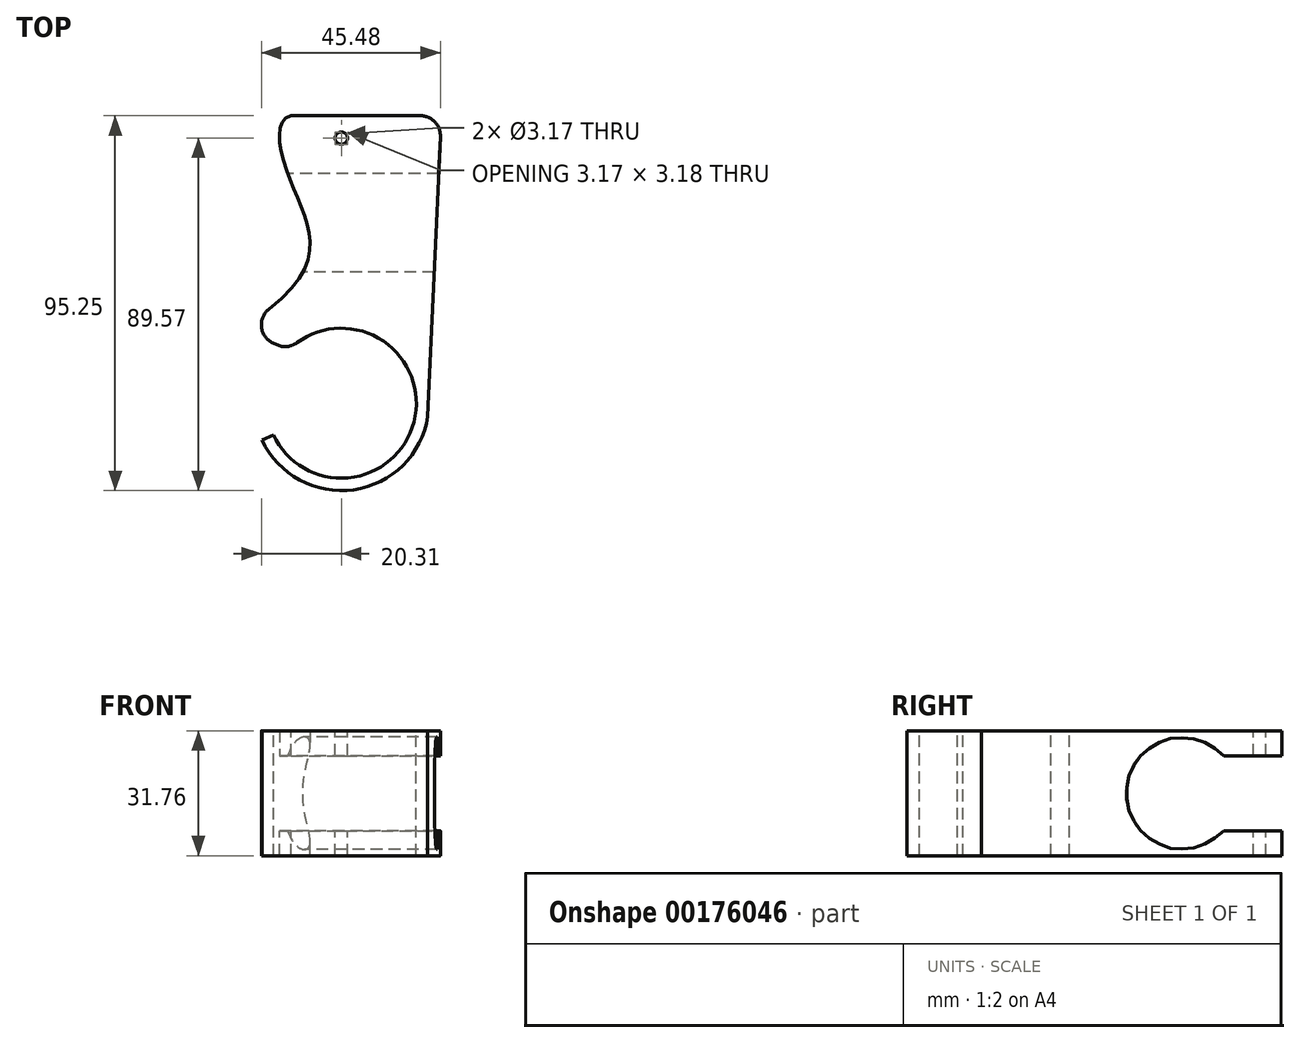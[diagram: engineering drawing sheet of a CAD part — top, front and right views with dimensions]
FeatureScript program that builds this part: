
annotation { "Feature Type Name" : "Feature", "Feature Type Description" : "" }
export const myFeature = defineFeature(function(context is Context, id is Id, definition is map)
    precondition{}
    {
        {
            var Q0;
            Q0=qCreatedBy(makeId("Right.planeOp"),FACE);
            var sketch = newSketch(context, id + "F0", { "sketchPlane" : qUnion([Q0])});
            skCircle(sketch, "E0", {"center": v(0, 0) * mm, "radius": 14.29 * mm});
            skSolve(sketch);
        }
        {
            var Q0;
            Q0=qCreatedBy(makeId("Right.planeOp"),FACE);
            var sketch = newSketch(context, id + "F1", { "sketchPlane" : qUnion([Q0])});
            skCircle(sketch, "E1", {"center": v(0, 0) * mm, "radius": 14.29 * mm});
            skLineSegment(sketch, "E2.bottom", {"start": v(-25.4, 15.88) * mm, "end": v(25.4, 15.88) * mm});
            skLineSegment(sketch, "E2.top", {"start": v(-25.4, -15.88) * mm, "end": v(25.4, -15.88) * mm});
            skLineSegment(sketch, "E2.left", {"start": v(-25.4, 15.88) * mm, "end": v(-25.4, -15.88) * mm});
            skLineSegment(sketch, "E2.right", {"start": v(25.4, 15.88) * mm, "end": v(25.4, -15.88) * mm});
            skCircle(sketch, "E3", {"center": v(0, 0) * mm, "radius": 15.88 * mm});
            skLineSegment(sketch, "E4", {"start": v(-28.58, 15.88) * mm, "end": v(-28.58, -15.88) * mm});
            skLineSegment(sketch, "E5", {"start": v(-25.4, 15.88) * mm, "end": v(-28.58, 15.88) * mm});
            skLineSegment(sketch, "E6", {"start": v(-28.58, -15.88) * mm, "end": v(-25.4, -15.88) * mm});
            skSolve(sketch);
        }
        {
            var Q0;
            {var subQ0=sQuery(id+"F1.wireOp",EDGE,"E2.right");Q0=makeQuery(id+"F1.imprint","IMPRINT",FACE,{"disambiguationData":[TD([[makeQuery(id+"F1.imprint","IMPRINT",EDGE,{"derivedFrom":subQ0}),-1.0]])]});}
            var Q1;
            {var subQ0=sQuery(id+"F1.wireOp",EDGE,"E2.bottom");var subQ1=sQuery(id+"F1.wireOp",EDGE,"E1");var subQ2=makeQuery(id+"F1.imprint","INTERSECT",VERTEX,{"derivedFrom":[subQ1,subQ0]});Q1=makeQuery(id+"F1.imprint","IMPRINT",FACE,{"disambiguationData":[TD([[makeQuery(id+"F1.imprint","IMPRINT",EDGE,{"disambiguationData":[TD([[subQ2,1.0]])],"derivedFrom":subQ1}),-1.0]])]});}
            var Q2;
            {var subQ0=sQuery(id+"F1.wireOp",EDGE,"E3");var subQ1=sQuery(id+"F1.wireOp",EDGE,"E2.bottom");var subQ2=makeQuery(id+"F1.imprint","INTERSECT",VERTEX,{"disambiguationData":[OD(0.0)],"derivedFrom":[subQ1,subQ0]});Q2=makeQuery(id+"F1.imprint","IMPRINT",FACE,{"disambiguationData":[TD([[makeQuery(id+"F1.imprint","IMPRINT",EDGE,{"disambiguationData":[TD([[subQ2,-1.0]])],"derivedFrom":subQ1}),1.0]])]});}
            var Q3;
            {var subQ0=sQuery(id+"F1.wireOp",EDGE,"E2.left");Q3=makeQuery(id+"F1.imprint","IMPRINT",FACE,{"disambiguationData":[TD([[makeQuery(id+"F1.imprint","IMPRINT",EDGE,{"derivedFrom":subQ0}),1.0]])]});}
            var Q4;
            {var subQ0=sQuery(id+"F1.wireOp",EDGE,"E3");var subQ1=sQuery(id+"F1.wireOp",EDGE,"E2.top");var subQ2=makeQuery(id+"F1.imprint","INTERSECT",VERTEX,{"disambiguationData":[OD(0.0)],"derivedFrom":[subQ1,subQ0]});Q4=makeQuery(id+"F1.imprint","IMPRINT",FACE,{"disambiguationData":[TD([[makeQuery(id+"F1.imprint","IMPRINT",EDGE,{"disambiguationData":[TD([[subQ2,-1.0]])],"derivedFrom":subQ1}),-1.0]])]});}
            var Q5;
            {var subQ0=sQuery(id+"F1.wireOp",EDGE,"E2.bottom");var subQ1=sQuery(id+"F1.wireOp",EDGE,"E1");var subQ2=makeQuery(id+"F1.imprint","INTERSECT",VERTEX,{"derivedFrom":[subQ1,subQ0]});Q5=makeQuery(id+"F1.imprint","IMPRINT",FACE,{"disambiguationData":[TD([[makeQuery(id+"F1.imprint","IMPRINT",EDGE,{"disambiguationData":[TD([[subQ2,-1.0]])],"derivedFrom":subQ1}),-1.0]])]});}
            var Q6;
            {var subQ0=sQuery(id+"F1.wireOp",EDGE,"E4");Q6=makeQuery(id+"F1.imprint","IMPRINT",FACE,{"disambiguationData":[TD([[makeQuery(id+"F1.imprint","IMPRINT",EDGE,{"derivedFrom":subQ0}),1.0]])]});}
            extrude(context, id + "F2", {"entities" : qUnion([Q0, Q1, Q2, Q3, Q4, Q5, Q6]), "endBound" : BoundingType.SYMMETRIC, "depth" : 50.8 * mm});
        }
        {
            var Q0;
            Q0=makeQuery(id+"F2.opExtrude","CAP_FACE",FACE,{"disambiguationData":[OSD([sQuery(id+"F1.wireOp",EDGE,"E1"),sQuery(id+"F1.wireOp",EDGE,"E2.bottom"),sQuery(id+"F1.wireOp",EDGE,"E2.top"),sQuery(id+"F1.wireOp",EDGE,"E2.left"),sQuery(id+"F1.wireOp",EDGE,"E2.right"),sQuery(id+"F1.wireOp",EDGE,"E3")])],"isStart":false});
            var sketch = newSketch(context, id + "F3", { "sketchPlane" : qUnion([Q0])});
            skLineSegment(sketch, "E7.bottom", {"start": v(0, 9.53) * mm, "end": v(25.4, 9.53) * mm});
            skLineSegment(sketch, "E7.top", {"start": v(0, -9.53) * mm, "end": v(25.4, -9.53) * mm});
            skLineSegment(sketch, "E7.left", {"start": v(0, 9.53) * mm, "end": v(0, -9.53) * mm});
            skLineSegment(sketch, "E7.right", {"start": v(25.4, 9.53) * mm, "end": v(25.4, -9.53) * mm});
            skPoint(sketch, "E7.middle", {"position": v(12.7, 0) * mm});
            skSolve(sketch);
        }
        {
            var Q0;
            {var subQ0=sQuery(id+"F3.wireOp",EDGE,"E7.left");Q0=makeQuery(id+"F3.imprint","IMPRINT",FACE,{"disambiguationData":[TD([[makeQuery(id+"F3.imprint","IMPRINT",EDGE,{"derivedFrom":subQ0}),1.0]])]});}
            var Q1;
            {var subQ0=sQuery(id+"F3.wireOp",EDGE,"E7.right");Q1=makeQuery(id+"F3.imprint","IMPRINT",FACE,{"disambiguationData":[TD([[makeQuery(id+"F3.imprint","IMPRINT",EDGE,{"derivedFrom":subQ0}),-1.0]])]});}
            extrude(context, id + "F4", {"entities" : qUnion([Q0, Q1]), "operationType" : NewBodyOperationType.REMOVE, "endBound" : BoundingType.THROUGH_ALL, "oppositeDirection" : true, "depth" : 25.4 * mm});
        }
        {
            var Q0;
            {var subQ0=sQuery(id+"F1.wireOp",EDGE,"E2.bottom");Q0=makeQuery(id+"F2.opExtrude","SWEPT_FACE",FACE,{"disambiguationData":[OSD([subQ0]),TDD([makeQuery(id+"F1.imprint","IMPRINT",EDGE,{"disambiguationData":[TD([[makeQuery(id+"F1.imprint","INTERSECT",VERTEX,{"derivedFrom":[subQ0,sQuery(id+"F1.wireOp",EDGE,"E4")]}),-1.0]])],"derivedFrom":subQ0})])]});}
            var sketch = newSketch(context, id + "F5", { "sketchPlane" : qUnion([Q0])});
            skCircle(sketch, "E8", {"center": v(0, -47.63) * mm, "radius": 19.05 * mm});
            skCircle(sketch, "E9", {"center": v(0, -47.63) * mm, "radius": 22.23 * mm});
            skLineSegment(sketch, "E10", {"start": v(0, -47.63) * mm, "end": v(-15.72, -31.9) * mm});
            skLineSegment(sketch, "E11", {"start": v(0, -47.63) * mm, "end": v(-20.14, -57.02) * mm});
            skSolve(sketch);
        }
        {
            var Q0;
            {var subQ0=sQuery(id+"F5.wireOp",EDGE,"E10");var subQ1=sQuery(id+"F5.wireOp",EDGE,"E9");var subQ2=makeQuery(id+"F5.imprint","INTERSECT",VERTEX,{"derivedFrom":[subQ1,subQ0]});Q0=makeQuery(id+"F5.imprint","IMPRINT",FACE,{"disambiguationData":[TD([[makeQuery(id+"F5.imprint","IMPRINT",EDGE,{"disambiguationData":[TD([[subQ2,1.0]])],"derivedFrom":subQ0}),-1.0]])]});}
            var Q1;
            {var subQ7=sQuery(id+"F5.wireOp",EDGE,"E11");var subQ8=sQuery(id+"F5.wireOp",EDGE,"E9");var subQ9=makeQuery(id+"F5.imprint","INTERSECT",VERTEX,{"derivedFrom":[subQ8,subQ7]});Q1=makeQuery(id+"F5.imprint","IMPRINT",FACE,{"disambiguationData":[TD([[makeQuery(id+"F5.imprint","IMPRINT",EDGE,{"disambiguationData":[TD([[subQ9,1.0]])],"derivedFrom":subQ7}),1.0]])]});}
            var Q2;
            {var subQ0=sQuery(id+"F1.wireOp",EDGE,"E2.top");Q2=makeQuery(id+"F2.opExtrude","SWEPT_FACE",FACE,{"disambiguationData":[OSD([subQ0]),TDD([makeQuery(id+"F1.imprint","IMPRINT",EDGE,{"disambiguationData":[TD([[makeQuery(id+"F1.imprint","INTERSECT",VERTEX,{"derivedFrom":[subQ0,sQuery(id+"F1.wireOp",EDGE,"E4")]}),-1.0]])],"derivedFrom":subQ0})])]});}
            extrude(context, id + "F6", {"entities" : qUnion([Q0, Q1]), "operationType" : NewBodyOperationType.ADD, "endBound" : BoundingType.UP_TO_SURFACE, "oppositeDirection" : true, "endBoundEntityFace" : qUnion([Q2]), "depth" : 25.4 * mm});
        }
        {
            var Q0;
            {var subQ0=sQuery(id+"F1.wireOp",EDGE,"E2.bottom");Q0=makeQuery(id+"F2.opExtrude","SWEPT_FACE",FACE,{"disambiguationData":[OSD([subQ0]),TDD([makeQuery(id+"F1.imprint","IMPRINT",EDGE,{"disambiguationData":[TD([[makeQuery(id+"F1.imprint","INTERSECT",VERTEX,{"derivedFrom":[subQ0,sQuery(id+"F1.wireOp",EDGE,"E2.right")]}),1.0]])],"derivedFrom":subQ0})])]});}
            var sketch = newSketch(context, id + "F7", { "sketchPlane" : qUnion([Q0])});
            skCircle(sketch, "E12", {"center": v(0, 19.72) * mm, "radius": 1.59 * mm});
            skSolve(sketch);
        }
        {
            var Q0;
            Q0=makeQuery(id+"F7.imprint","IMPRINT",FACE,{"disambiguationData":[TD([[makeQuery(id+"F7.imprint","IMPRINT",EDGE,{"derivedFrom":sQuery(id+"F7.wireOp",EDGE,"E12")}),1.0]])]});
            extrude(context, id + "F8", {"entities" : qUnion([Q0]), "operationType" : NewBodyOperationType.REMOVE, "endBound" : BoundingType.THROUGH_ALL, "oppositeDirection" : true, "depth" : 25.4 * mm});
        }
        {
            var Q0;
            {var subQ0=sQuery(id+"F5.wireOp",EDGE,"E9");var subQ1=sQuery(id+"F5.wireOp",EDGE,"E8");var subQ2=sQuery(id+"F1.wireOp",EDGE,"E5");var subQ3=sQuery(id+"F1.wireOp",EDGE,"E4");Q0=makeQuery(id+"F6.boolean.opBoolean","MERGE",FACE,{"derivedFrom":[makeQuery(id+"F2.opExtrude","SWEPT_FACE",FACE,{"disambiguationData":[OSD([sQuery(id+"F1.wireOp",EDGE,"E2.bottom"),subQ2])]}),makeQuery(id+"F6.opExtrude","CAP_FACE",FACE,{"disambiguationData":[OSD([subQ3,subQ2,subQ1,subQ0,sQuery(id+"F5.wireOp",EDGE,"E10")])],"isStart":true}),makeQuery(id+"F6.opExtrude","CAP_FACE",FACE,{"disambiguationData":[OSD([subQ3,subQ2,subQ1,subQ0,sQuery(id+"F5.wireOp",EDGE,"E11")])],"isStart":true})]});}
            var sketch = newSketch(context, id + "F9", { "sketchPlane" : qUnion([Q0])});
            skLineSegment(sketch, "E13", {"start": v(25.4, -28.58) * mm, "end": v(21.97, -50.99) * mm});
            skLineSegment(sketch, "E14", {"start": v(-25.4, -28.58) * mm, "end": v(-13.47, -34.15) * mm});
            skSolve(sketch);
        }
        {
            var Q0;
            Q0 = qSketchRegion(id + "F9", true);
            var Q1;
            {var subQ1=sQuery(id+"F5.wireOp",EDGE,"E10");var subQ2=sQuery(id+"F5.wireOp",EDGE,"E9");var subQ4=sQuery(id+"F1.wireOp",EDGE,"E5");var subQ5=sQuery(id+"F1.wireOp",EDGE,"E4");var subQ6=makeQuery(id+"F2.opExtrude","SWEPT_EDGE",EDGE,{"disambiguationData":[OSD([subQ5,subQ4])]});var subQ7=makeQuery(id+"F5.imprint","IMPRINT",EDGE,{"disambiguationData":[TD([[makeQuery(id+"F5.imprint","INTERSECT",VERTEX,{"derivedFrom":[subQ2,subQ1]}),1.0]])],"derivedFrom":subQ2});var subQ9=makeQuery(id+"F6.boolean.opBoolean","SPLIT",EDGE,{"disambiguationData":[TD([makeQuery(id+"F6.opExtrude","SWEPT_FACE",FACE,{"disambiguationData":[OSD([subQ2]),TDD([subQ7])]})])],"derivedFrom":subQ6});Q1=makeQuery(id+"F9.imprint","IMPRINT",FACE,{"disambiguationData":[TD([[makeQuery(id+"F9.imprint","IMPRINT",EDGE,{"derivedFrom":subQ9}),1.0]])]});}
            var Q2;
            {var subQ0=sQuery(id+"F9.wireOp",EDGE,"E13");Q2=makeQuery(id+"F9.imprint","IMPRINT",FACE,{"disambiguationData":[TD([[makeQuery(id+"F9.imprint","IMPRINT",EDGE,{"derivedFrom":subQ0}),-1.0]])]});}
            var Q3;
            {var subQ0=sQuery(id+"F5.wireOp",EDGE,"E9");var subQ1=sQuery(id+"F5.wireOp",EDGE,"E8");var subQ2=sQuery(id+"F1.wireOp",EDGE,"E5");var subQ3=sQuery(id+"F1.wireOp",EDGE,"E4");var subQ4=sQuery(id+"F1.wireOp",EDGE,"E6");var subQ5=sQuery(id+"F1.wireOp",EDGE,"E2.top");Q3=makeQuery(id+"F6.boolean.opBoolean","MERGE",FACE,{"derivedFrom":[makeQuery(id+"F2.opExtrude","SWEPT_FACE",FACE,{"disambiguationData":[OSD([subQ5,subQ4])]}),makeQuery(id+"F6.opExtrude","CAP_FACE",FACE,{"disambiguationData":[OSD([subQ5,subQ4]),ownerDisambiguation([makeQuery(id+"F6.opExtrude","SWEPT_BODY",BODY,{"disambiguationData":[OSD([subQ3,subQ2,subQ1,subQ0,sQuery(id+"F5.wireOp",EDGE,"E10")])]})])],"isStart":false}),makeQuery(id+"F6.opExtrude","CAP_FACE",FACE,{"disambiguationData":[OSD([subQ5,subQ4]),ownerDisambiguation([makeQuery(id+"F6.opExtrude","SWEPT_BODY",BODY,{"disambiguationData":[OSD([subQ3,subQ2,subQ1,subQ0,sQuery(id+"F5.wireOp",EDGE,"E11")])]})])],"isStart":false})]});}
            extrude(context, id + "F10", {"entities" : qUnion([Q0, Q1, Q2]), "operationType" : NewBodyOperationType.ADD, "endBound" : BoundingType.UP_TO_SURFACE, "oppositeDirection" : true, "endBoundEntityFace" : qUnion([Q3]), "depth" : 25.4 * mm});
        }
        {
            var Q0;
            {var subQ0=sQuery(id+"F5.wireOp",EDGE,"E9");var subQ1=sQuery(id+"F1.wireOp",EDGE,"E5");var subQ2=sQuery(id+"F1.wireOp",EDGE,"E4");var subQ3=sQuery(id+"F5.wireOp",EDGE,"E8");Q0=makeQuery(id+"F10.boolean.opBoolean","MERGE",FACE,{"derivedFrom":[makeQuery(id+"F6.boolean.opBoolean","MERGE",FACE,{"derivedFrom":[makeQuery(id+"F2.opExtrude","SWEPT_FACE",FACE,{"disambiguationData":[OSD([sQuery(id+"F1.wireOp",EDGE,"E2.bottom"),subQ1])]}),makeQuery(id+"F6.opExtrude","CAP_FACE",FACE,{"disambiguationData":[OSD([subQ2,subQ1,subQ3,subQ0,sQuery(id+"F5.wireOp",EDGE,"E10")])],"isStart":true}),makeQuery(id+"F6.opExtrude","CAP_FACE",FACE,{"disambiguationData":[OSD([subQ2,subQ1,subQ3,subQ0,sQuery(id+"F5.wireOp",EDGE,"E11")])],"isStart":true})]}),makeQuery(id+"F10.opExtrude","CAP_FACE",FACE,{"disambiguationData":[OSD([subQ2,subQ1,subQ0,sQuery(id+"F9.wireOp",EDGE,"vnx9pd8C-HjGg-3WXh-8BVK-Msj8Zm1Jhp6u")])],"isStart":true}),makeQuery(id+"F10.opExtrude","CAP_FACE",FACE,{"disambiguationData":[OSD([subQ2,subQ1,subQ0,sQuery(id+"F9.wireOp",EDGE,"E13")])],"isStart":true})]});}
            var sketch = newSketch(context, id + "F11", { "sketchPlane" : qUnion([Q0])});
            skLineSegment(sketch, "E15", {"start": v(25.4, 25.4) * mm, "end": v(21.97, -50.99) * mm});
            skSolve(sketch);
        }
        {
            var Q0;
            Q0 = qSketchRegion(id + "F11", true);
            var Q1;
            Q1=makeQuery(id+"F11.imprint","IMPRINT",FACE,{"disambiguationData":[TD([[makeQuery(id+"F11.imprint","IMPRINT",EDGE,{"derivedFrom":sQuery(id+"F11.wireOp",EDGE,"pskV8I0j-hnk2-iIVi-R23I-b5Myljy8wFEx")}),-1.0]])]});
            var Q2;
            Q2=makeQuery(id+"F11.imprint","IMPRINT",FACE,{"disambiguationData":[TD([[makeQuery(id+"F11.imprint","IMPRINT",EDGE,{"derivedFrom":sQuery(id+"F11.wireOp",EDGE,"E15")}),1.0]])]});
            extrude(context, id + "F12", {"entities" : qUnion([Q0, Q1, Q2]), "operationType" : NewBodyOperationType.REMOVE, "endBound" : BoundingType.THROUGH_ALL, "oppositeDirection" : true, "depth" : 25.4 * mm});
        }
        {
            var Q0;
            {var subQ0=sQuery(id+"F5.wireOp",EDGE,"E10");var subQ1=sQuery(id+"F5.wireOp",EDGE,"E8");Q0=makeQuery(id+"F10.boolean.opBoolean","MERGE",EDGE,{"derivedFrom":[makeQuery(id+"F6.opExtrude","SWEPT_EDGE",EDGE,{"disambiguationData":[OSD([subQ1,subQ0])]}),makeQuery(id+"F10.opExtrude","SWEPT_EDGE",EDGE,{"disambiguationData":[OSD([subQ1,subQ0,sQuery(id+"F9.wireOp",EDGE,"E14")])]})]});}
            fillet(context, id + "F13", {"entities" : qUnion([Q0]), "radius" : 5.08 * mm, "tangentPropagation" : true, "allowEdgeOverflow" : false});
        }
        {
            var Q0;
            {var subQ0=sQuery(id+"F5.wireOp",EDGE,"E10");var subQ1=sQuery(id+"F5.wireOp",EDGE,"E9");var subQ2=sQuery(id+"F1.wireOp",EDGE,"E5");var subQ3=sQuery(id+"F1.wireOp",EDGE,"E4");var subQ4=sQuery(id+"F5.wireOp",EDGE,"E8");Q0=makeQuery(id+"F10.boolean.opBoolean","MERGE",FACE,{"derivedFrom":[makeQuery(id+"F6.boolean.opBoolean","MERGE",FACE,{"derivedFrom":[makeQuery(id+"F2.opExtrude","SWEPT_FACE",FACE,{"disambiguationData":[OSD([sQuery(id+"F1.wireOp",EDGE,"E2.bottom"),subQ2])]}),makeQuery(id+"F6.opExtrude","CAP_FACE",FACE,{"disambiguationData":[OSD([subQ3,subQ2,subQ4,subQ1,subQ0])],"isStart":true}),makeQuery(id+"F6.opExtrude","CAP_FACE",FACE,{"disambiguationData":[OSD([subQ3,subQ2,subQ4,subQ1,sQuery(id+"F5.wireOp",EDGE,"E11")])],"isStart":true})]}),makeQuery(id+"F10.opExtrude","CAP_FACE",FACE,{"disambiguationData":[OSD([subQ3,subQ2,subQ1,sQuery(id+"F9.wireOp",EDGE,"E13")])],"isStart":true}),makeQuery(id+"F10.opExtrude","CAP_FACE",FACE,{"disambiguationData":[OSD([subQ3,subQ2,subQ1,subQ0,sQuery(id+"F9.wireOp",EDGE,"E14")])],"isStart":true})]});}
            var sketch = newSketch(context, id + "F14", { "sketchPlane" : qUnion([Q0])});
            skFitSpline(sketch, "E16", {"points": [v(-11.59, 25.56) * mm, v(-12.62, 8.06) * mm, v(-25.4, -28.58) * mm], "startDerivative": vector(-48.35, -1.23) * mm, "endDerivative": vector(-122.94, -76.25) * mm});
            skSolve(sketch);
        }
        {
            var Q0;
            Q0=makeQuery(id+"F14.imprint","IMPRINT",FACE,{"disambiguationData":[TD([[makeQuery(id+"F14.imprint","IMPRINT",EDGE,{"derivedFrom":sQuery(id+"F14.wireOp",EDGE,"E16")}),-1.0]])]});
            extrude(context, id + "F15", {"entities" : qUnion([Q0]), "operationType" : NewBodyOperationType.REMOVE, "endBound" : BoundingType.THROUGH_ALL, "oppositeDirection" : true, "depth" : 25.4 * mm});
        }
        {
            var Q0;
            {var subQ0=sQuery(id+"F9.wireOp",EDGE,"E14");var subQ1=sQuery(id+"F1.wireOp",EDGE,"E5");var subQ2=sQuery(id+"F1.wireOp",EDGE,"E2.bottom");var subQ3=sQuery(id+"F1.wireOp",EDGE,"E4");Q0=makeQuery(id+"F15.boolean.opBoolean","MERGE",EDGE,{"derivedFrom":[makeQuery(id+"F10.boolean.opBoolean","MERGE",EDGE,{"derivedFrom":[makeQuery(id+"F2.opExtrude","CAP_EDGE",EDGE,{"disambiguationData":[OSD([subQ3])],"isStart":true}),makeQuery(id+"F10.opExtrude","SWEPT_EDGE",EDGE,{"disambiguationData":[OSD([subQ2,subQ3,subQ1,subQ0])]})]}),makeQuery(id+"F15.opExtrude","SWEPT_EDGE",EDGE,{"disambiguationData":[OSD([subQ2,subQ1,subQ0,sQuery(id+"F14.wireOp",EDGE,"E16")])]})]});}
            fillet(context, id + "F16", {"entities" : qUnion([Q0]), "radius" : 5.08 * mm, "tangentPropagation" : true, "allowEdgeOverflow" : false});
        }
        {
            var Q0;
            {var subQ0=sQuery(id+"F1.wireOp",EDGE,"E5");var subQ1=sQuery(id+"F1.wireOp",EDGE,"E2.right");var subQ2=sQuery(id+"F1.wireOp",EDGE,"E2.bottom");Q0=makeQuery(id+"F12.boolean.opBoolean","MERGE",EDGE,{"derivedFrom":[makeQuery(id+"F4.boolean.opBoolean","SPLIT",EDGE,{"disambiguationData":[TD([makeQuery(id+"F4.opExtrude","SWEPT_FACE",FACE,{"disambiguationData":[OSD([sQuery(id+"F3.wireOp",EDGE,"E7.bottom")])]})])],"derivedFrom":makeQuery(id+"F2.opExtrude","CAP_EDGE",EDGE,{"disambiguationData":[OSD([subQ1])],"isStart":false})}),makeQuery(id+"F12.opExtrude","SWEPT_EDGE",EDGE,{"disambiguationData":[OSD([subQ2,subQ1,subQ0,sQuery(id+"F11.wireOp",EDGE,"E15")])]})]});}
            var Q1;
            {var subQ0=sQuery(id+"F1.wireOp",EDGE,"E5");var subQ1=sQuery(id+"F1.wireOp",EDGE,"E2.right");var subQ2=sQuery(id+"F1.wireOp",EDGE,"E2.bottom");Q1=makeQuery(id+"F12.boolean.opBoolean","MERGE",EDGE,{"derivedFrom":[makeQuery(id+"F4.boolean.opBoolean","SPLIT",EDGE,{"disambiguationData":[TD([makeQuery(id+"F4.opExtrude","SWEPT_FACE",FACE,{"disambiguationData":[OSD([sQuery(id+"F3.wireOp",EDGE,"E7.top")])]})])],"derivedFrom":makeQuery(id+"F2.opExtrude","CAP_EDGE",EDGE,{"disambiguationData":[OSD([subQ1])],"isStart":false})}),makeQuery(id+"F12.opExtrude","SWEPT_EDGE",EDGE,{"disambiguationData":[OSD([subQ2,subQ1,subQ0,sQuery(id+"F11.wireOp",EDGE,"E15")])]})]});}
            fillet(context, id + "F17", {"entities" : qUnion([Q0, Q1]), "radius" : 5.08 * mm, "tangentPropagation" : true, "allowEdgeOverflow" : false});
        }
    });
